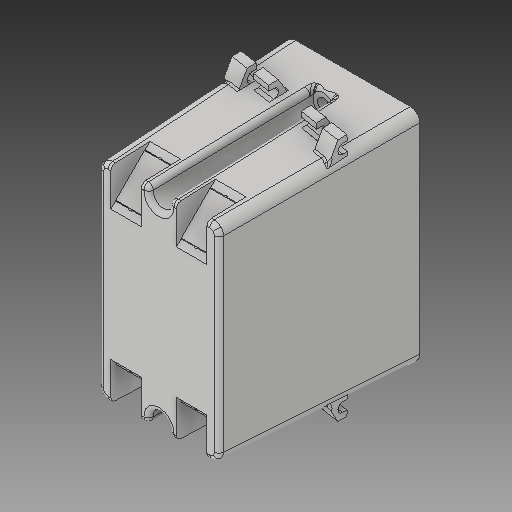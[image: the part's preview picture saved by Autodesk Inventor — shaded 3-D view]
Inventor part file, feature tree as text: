
AUTODESK INVENTOR PART (.ipt)
format: ipt  version: 2018 (Build 220112000, 112)  size: 694,272 bytes
history: native  units: in
note: dims shown in document units (in); Inventor stores cm internally (conversion verified against a paired STEP export)
features: fillet x1
ambient origin geometry x8: Origin, YZ Plane, XZ Plane, XY Plane, X Axis, Y Axis, Z Axis, Center Point
bodies: Solid1 (feature_tree)
feature tree (1):
  fillet  "Fillet21"  [1 undecoded]
note: 1 required parameter value undecoded (feature->parameter linkage not recoverable at this tier; creation-order binding heuristic only, values carry confidence <= 0.55)
